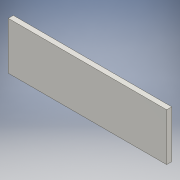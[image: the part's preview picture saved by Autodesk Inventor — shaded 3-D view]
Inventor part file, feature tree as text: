
AUTODESK INVENTOR PART (.ipt)
format: ipt  version: 2018 (Build 220112000, 112)  size: 90,112 bytes
history: native  units: mm
features: extrude x1, sketch x1
ambient origin geometry x8: Origin, YZ Plane, XZ Plane, XY Plane, X Axis, Y Axis, Z Axis, Center Point
bodies: Solid1 (feature_tree)
feature tree (2):
  extrude  "Extrusion1"  Depth=15.0mm
  sketch  "Sketch1"  dims[d0=50.0mm d1=15.0mm d2=1.6mm d3=0.0mm]
